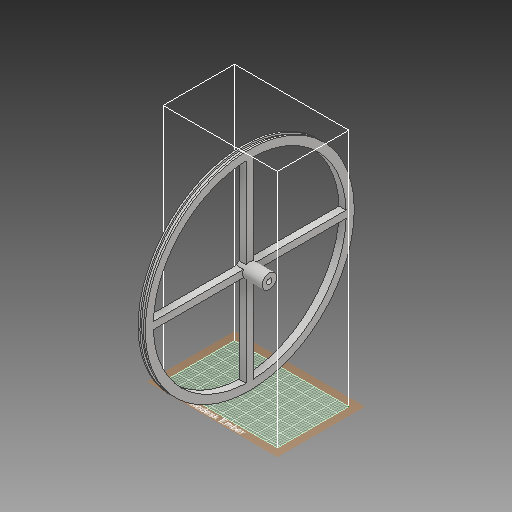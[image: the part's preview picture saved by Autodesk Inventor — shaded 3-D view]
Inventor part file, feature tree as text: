
AUTODESK INVENTOR PART (.ipt)
format: ipt  version: 2018 (Build 220112000, 112)  size: 334,848 bytes
history: native  units: mm
features: extrude x8, sketch x8, pattern_circular x1
ambient origin geometry x8: Origin, YZ Plane, XZ Plane, XY Plane, X Axis, Y Axis, Z Axis, Center Point
bodies: Solid1 (feature_tree)
feature tree (17):
  extrude  "Extrusion1"  Depth=2.0mm TaperAngle=0.0deg
  extrude  "Extrusion2"  Depth=1.0mm TaperAngle=0.0deg
  extrude  "Extrusion3"  Depth=1.0mm
  extrude  "Extrusion4"  Depth=3.0mm
  extrude  "Extrusion5"  Depth=5.0mm TaperAngle=0.0deg
  extrude  "Extrusion6"  Depth=4.0mm
  pattern_circular  "Circular Pattern1"  Count=4 Angle=360.0deg
  extrude  "Extrusion7"  Depth=15.0mm TaperAngle=0.0deg
  extrude  "Extrusion8"  Depth=15.0mm
  sketch  "Sketch1"  dims[d0=115.0mm d1=2.0mm d2=0.0mm]
  sketch  "Sketch2"  dims[d3=117.0mm d4=1.0mm d5=0.0mm]
  sketch  "Sketch3"  dims[d6=1.0mm d7=0.0mm d8=108.0mm]
  sketch  "Sketch4"  dims[d9=5.0mm d10=0.0mm d11=3.0mm]
  sketch  "Sketch5"  dims[d12=7.0mm d13=5.0mm d14=0.0mm]
  sketch  "Sketch6"  dims[d15=2.0mm d16=4.0mm]
  sketch  "Sketch7"  dims[d17=4.0mm d18=0.0mm d19=40.0mm d20=360.0deg]
  sketch  "Sketch8"  dims[d22=8.0mm d23=15.0mm d24=0.0mm d25=3.25mm d26=100.0mm d27=0.0mm]
